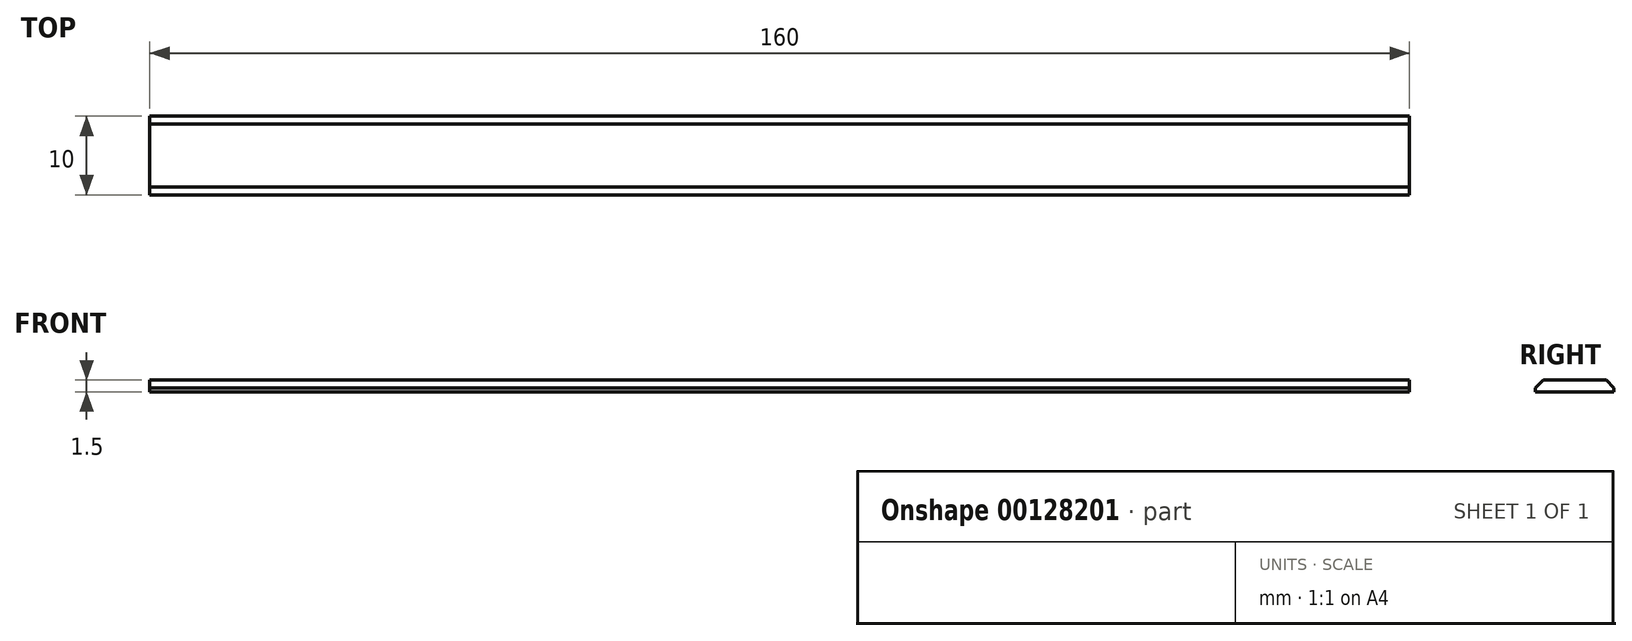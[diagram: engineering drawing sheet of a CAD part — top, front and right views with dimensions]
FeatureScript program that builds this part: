
annotation { "Feature Type Name" : "Feature", "Feature Type Description" : "" }
export const myFeature = defineFeature(function(context is Context, id is Id, definition is map)
    precondition{}
    {
        {
            var Q0;
            Q0=qCreatedBy(makeId("Top.planeOp"),FACE);
            var sketch = newSketch(context, id + "F0", { "sketchPlane" : qUnion([Q0])});
            skLineSegment(sketch, "E0.bottom", {"start": v(80, -5) * mm, "end": v(-80, -5) * mm});
            skLineSegment(sketch, "E0.top", {"start": v(80, 5) * mm, "end": v(-80, 5) * mm});
            skLineSegment(sketch, "E0.left", {"start": v(80, -5) * mm, "end": v(80, 5) * mm});
            skLineSegment(sketch, "E0.right", {"start": v(-80, -5) * mm, "end": v(-80, 5) * mm});
            skPoint(sketch, "E0.middle", {"position": v(0, 0) * mm});
            skSolve(sketch);
        }
        {
            var Q0;
            Q0 = qSketchRegion(id + "F0", true);
            extrude(context, id + "F1", {"entities" : qUnion([Q0]), "depth" : 1.5 * mm});
        }
        {
            var Q0;
            Q0=makeQuery(id+"F1.opExtrude","CAP_EDGE",EDGE,{"disambiguationData":[OSD([sQuery(id+"F0.wireOp",EDGE,"E0.bottom")])],"isStart":false});
            var Q1;
            Q1=makeQuery(id+"F1.opExtrude","CAP_EDGE",EDGE,{"disambiguationData":[OSD([sQuery(id+"F0.wireOp",EDGE,"E0.top")])],"isStart":false});
            chamfer(context, id + "F2", {"entities" : qUnion([Q0, Q1]), "width" : 1 * mm, "tangentPropagation" : true});
        }
    });
